# Revit family: NLRS_57_DUA_UN_Rectangular_Variable_volume_damper_LT_VRVxSxx_Solid_Air
name_source: partatom
category: Duct Accessories
revit_build: Autodesk Revit 2018 (Build: 20190510_1515(x64)
units: mm (PartAtom-declared; Revit-internal decimal feet)

## family parameters
Always vertical = No
Cut with Voids When Loaded = No
Part Type = Breaks Into
Round Connector Dimension = Use Diameter
Shared = No
Work Plane-Based = No

## types (1)
- VRVxSxx
    Article_Codes = VRV_Article_Codes
    Article_Data = VRV_Article_Data
    Assembly Code = 57.70
    Casing material = Galvanized Steel
    Description = Rechthoekige Variabel Volumeregelaar
    FireRating = 0h
    IfcDescription = Rechthoekige Variabel Volumeregelaar
    IfcExportAs = IfcDamperType
    IfcExportType = CONTROLDAMPER
    LoadBearing = No
    Manufacturer = Solid Air Climate Solutions
    Model = Variabel Volumeregelaar - Rechthoekig
    NLRS_C_content_datum_uitgifte = 24-04-2020
    NLRS_C_content_provider = Solid Air Climate Systems
    NLRS_C_content_versie = Versie 1.72
    NLRS_C_description = Rechthoekige Variabel Volumeregelaar
    NLRS_C_niveau ontwikkeling = LOD400
    SACS_AX_Prefix = 920
    SACS_Dummy = 1
    Type Comments = Check flow direction!
    URL = https://solid-air.nl

## geometry (parser evidence)
native form markers: Sweep x10
no freeform markers — native parametric forms only
